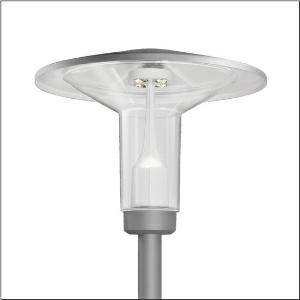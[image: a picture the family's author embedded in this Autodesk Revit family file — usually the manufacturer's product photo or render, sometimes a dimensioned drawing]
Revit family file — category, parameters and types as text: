
# Revit family: laterne_iq___st1_2a_5xa5255mf14h_e85f
name_source: partatom
category: Lighting Fixtures
units: mm (PartAtom-declared; Revit-internal decimal feet)

## family parameters
Cut with Voids When Loaded = No
Host = Face
Light Source = No
Part Type = Normal
Room Calculation Point = No
Round Connector Dimension = Use Diameter
Shared = No

## types (1)
- --- (1 x LED, 1540 lm, 11.8 W, 2700K)
    Apparent Load = 12 VA
    CIE Flux Codes = 25 63 94 98 100
    Color Rendering = 70
    Color Temperature = 2700K
    Default Elevation = 1800 mm
    Description = Lantern iQ, mast luminaire, Module 540 iQ-SR, primary light control with 3 zone facetted reflector, of plastic, silver coated, highly specular, structured, primary optical cover: cover, of PMMA, transparent, light distribution: ST1.2a, light emission: direct distribution, primary light characteristic: asymmetric, installation type: post-top, LED, High Power LED, rated luminous flux: 1.540lm, luminous efficacy: 131lm/W, light colour: 727, colour temperature: 2700K, control gear: ECG iQ, control: presetting dimming logarithmic, Street-Remote, Auto-Match, Temp-Guard, Lumen-Switch, Night-Set, Smart-Wire, Light-Fading, Desk-Remote (wireless, voltage-free reading and setting of iQ features in the workshop via application-optimized NFC function/RFID function), optimised constant luminous flux control (CLO 2.0), with terminal, 6-pole, max. 2.5mm², mains connection: 230..240V, AC, 50/60Hz, start of lifetime: 12W, end of service life: 12W, reduction: 6W, luminaire housing, upper part, of glass-fibre reinforced polyester, coated, Siteco® metallic grey (DB 702S), diameter: 750mm, height: 583mm, spigot size: d x l = 76 x 70mm (post-top) | with reducer (optional accessory) 60 x 70mm, post-top mast mounting element, of diecast aluminium, coated, Siteco® metallic grey (DB 702S), Module 540 iQ-SR, traffic white (RAL 9016), equipment: standard, protection rating (complete): IP65, insulation class (complete): insulation class II (safety insulation), certification: CE, ENEC, VDE, packaging unit: 1 piece

Light Distribution: ST1.2a
    Height = 583 mm
    Lamp = 1 x LED
    Lamp Light Flux = 1540 lm
    Lamp Power = 11.8 W
    Lamp count = 1
    Length = 750 mm
    Luminous efficacy = 131 lm/W
    Manufacturer = Siteco
    ModVariant = No
    Model = 5XA5255MF14H
    Number of Poles = 1
    OnlyDefault = Yes
    Power Factor = 1
    Product Name = Laterne iQ | ST1.2a
    Product group = mast luminaire | pylon top
    ProductGroupID = 6100
    Protection Class = Protection class II
    Protection Degree = IP 65
    RLX_Detail_Level = 1
    RLX_Emergency_Light_Flux = 0 lm
    RLX_Emergency_Type = 0
    RLX_Emergency_Type_DB = No
    RlxData = <blob elided: 103169 chars, md5=fa0b145c>
    Socket = socket
    Standby Power = 0 W
    System Light Flux = 1540 lm
    System Power = 12 W
    Type Comments = factory setting: luminous flux: 100 % | dim-lin: 254 | 472 mA
    Type Image = l_1006050.jpg
    URL = http://relux.com
    VarID = @adj_103563
    Voltage = 0 V
    Weight = 0.00 kg
    Width = 0 mm  [stored 0 ft]

note: [stored X ft] marks values corroborated as IEEE doubles in the binary element streams (Revit-internal decimal feet)

## geometry (parser evidence)
native form markers: Blend x4, Sweep x11
no freeform markers — native parametric forms only
